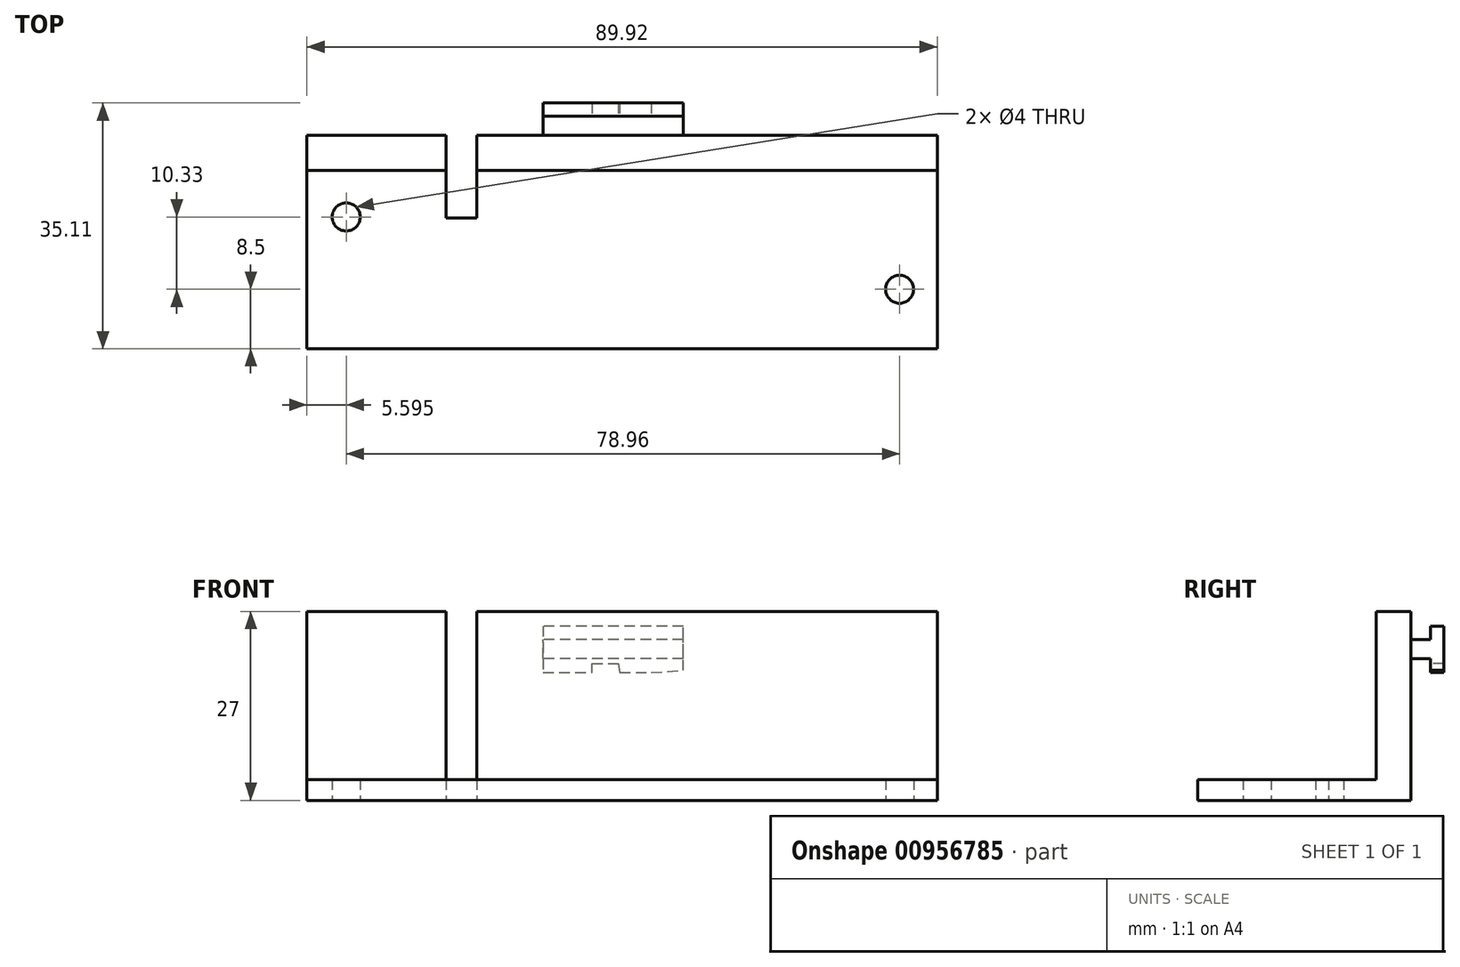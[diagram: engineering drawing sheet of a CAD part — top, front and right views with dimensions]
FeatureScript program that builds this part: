
annotation { "Feature Type Name" : "Feature", "Feature Type Description" : "" }
export const myFeature = defineFeature(function(context is Context, id is Id, definition is map)
    precondition{}
    {
        {
            var Q0;
            Q0=qCreatedBy(makeId("Top.planeOp"),FACE);
            var sketch = newSketch(context, id + "F0", { "sketchPlane" : qUnion([Q0])});
            skLineSegment(sketch, "E0.bottom", {"start": v(44.97, -13.73) * mm, "end": v(-44.97, -13.73) * mm});
            skLineSegment(sketch, "E0.top", {"start": v(44.97, 13.73) * mm, "end": v(-20.76, 13.73) * mm});
            skLineSegment(sketch, "E0.left", {"start": v(44.97, -13.73) * mm, "end": v(44.97, 13.73) * mm});
            skLineSegment(sketch, "E0.right", {"start": v(-44.97, -13.73) * mm, "end": v(-44.97, 13.73) * mm});
            skPoint(sketch, "E0.middle", {"position": v(0, 0) * mm});
            skLineSegment(sketch, "E1", {"start": v(-20.76, 13.73) * mm, "end": v(-20.76, 4.94) * mm});
            skLineSegment(sketch, "E2", {"start": v(-20.76, 4.94) * mm, "end": v(-25.1, 4.94) * mm});
            skLineSegment(sketch, "E3", {"start": v(-25.1, 4.94) * mm, "end": v(-25.1, 13.73) * mm});
            skLineSegment(sketch, "E4.trimOffspring", {"start": v(-25.1, 13.73) * mm, "end": v(-44.97, 13.73) * mm});
            skCircle(sketch, "E5", {"center": v(39.6, -5.23) * mm, "radius": 2 * mm});
            skCircle(sketch, "E6", {"center": v(-39.37, 5.1) * mm, "radius": 2 * mm});
            skSolve(sketch);
        }
        {
            var Q0;
            Q0=makeQuery(id+"F0.imprint","IMPRINT",FACE,{"disambiguationData":[TD([[makeQuery(id+"F0.imprint","IMPRINT",EDGE,{"derivedFrom":sQuery(id+"F0.wireOp",EDGE,"E0.bottom")}),-1.0]])]});
            extrude(context, id + "F1", {"entities" : qUnion([Q0]), "depth" : 3 * mm, "offsetDistance" : 25 * mm});
        }
        {
            var Q0;
            Q0=makeQuery(id+"F1.opExtrude","SWEPT_FACE",FACE,{"disambiguationData":[OSD([sQuery(id+"F0.wireOp",EDGE,"E4.trimOffspring")])]});
            var sketch = newSketch(context, id + "F2", { "sketchPlane" : qUnion([Q0])});
            skLineSegment(sketch, "E7.0", {"start": v(25.1, 0) * mm, "end": v(44.97, 0) * mm});
            skLineSegment(sketch, "E7.1", {"start": v(25.1, 3) * mm, "end": v(44.97, 3) * mm});
            skLineSegment(sketch, "E8", {"start": v(-8.73, 0) * mm, "end": v(-8.73, 3) * mm});
            skLineSegment(sketch, "E9", {"start": v(11.27, 0) * mm, "end": v(11.27, 3) * mm});
            skLineSegment(sketch, "E10.0", {"start": v(-44.97, 3) * mm, "end": v(-44.97, 0) * mm});
            skLineSegment(sketch, "E11.0", {"start": v(44.97, 3) * mm, "end": v(44.97, 0) * mm});
            skLineSegment(sketch, "E12.0", {"start": v(20.76, 0) * mm, "end": v(25.1, 0) * mm});
            skLineSegment(sketch, "E13.0", {"start": v(-44.97, 0) * mm, "end": v(20.76, 0) * mm});
            skLineSegment(sketch, "E14", {"start": v(44.97, 3) * mm, "end": v(44.97, 27) * mm});
            skLineSegment(sketch, "E15", {"start": v(44.97, 27) * mm, "end": v(-44.97, 27) * mm});
            skLineSegment(sketch, "E16", {"start": v(-44.97, 27) * mm, "end": v(-44.97, 3) * mm});
            skLineSegment(sketch, "E17.0", {"start": v(20.76, 3) * mm, "end": v(25.1, 3) * mm});
            skLineSegment(sketch, "E18.0", {"start": v(20.76, 3) * mm, "end": v(20.76, 0) * mm});
            skLineSegment(sketch, "E19", {"start": v(20.76, 3) * mm, "end": v(20.76, 27) * mm});
            skLineSegment(sketch, "E20", {"start": v(25.1, 3) * mm, "end": v(25.1, 27) * mm});
            skSolve(sketch);
        }
        {
            var Q0;
            {var subQ3=sQuery(id+"F2.wireOp",EDGE,"E10.0");Q0=makeQuery(id+"F2.imprint","IMPRINT",FACE,{"disambiguationData":[TD([[makeQuery(id+"F2.imprint","IMPRINT",EDGE,{"derivedFrom":subQ3}),1.0]])]});}
            var Q1;
            Q1=makeQuery(id+"F2.imprint","IMPRINT",FACE,{"disambiguationData":[TD([[makeQuery(id+"F2.imprint","IMPRINT",EDGE,{"derivedFrom":sQuery(id+"F2.wireOp",EDGE,"E7.1")}),1.0]])]});
            var Q2;
            Q2=makeQuery(id+"F2.imprint","IMPRINT",FACE,{"disambiguationData":[TD([[makeQuery(id+"F2.imprint","IMPRINT",EDGE,{"derivedFrom":sQuery(id+"F2.wireOp",EDGE,"E7.0")}),1.0]])]});
            extrude(context, id + "F3", {"entities" : qUnion([Q0, Q1, Q2]), "operationType" : NewBodyOperationType.ADD, "depth" : 3 * mm, "offsetDistance" : 25 * mm});
        }
        {
            var Q0;
            Q0=makeQuery(id+"F3.opExtrude","CAP_FACE",FACE,{"disambiguationData":[OSD([sQuery(id+"F0.wireOp",EDGE,"E3"),sQuery(id+"F0.wireOp",EDGE,"E4.trimOffspring"),sQuery(id+"F2.wireOp",EDGE,"E7.0"),sQuery(id+"F2.wireOp",EDGE,"E11.0"),sQuery(id+"F2.wireOp",EDGE,"E14"),sQuery(id+"F2.wireOp",EDGE,"E15"),sQuery(id+"F2.wireOp",EDGE,"E20")])],"isStart":false});
            var sketch = newSketch(context, id + "F4", { "sketchPlane" : qUnion([Q0])});
            skLineSegment(sketch, "E21.0", {"start": v(-8.73, 0) * mm, "end": v(-8.73, 3) * mm});
            skLineSegment(sketch, "E22.0", {"start": v(11.27, 0) * mm, "end": v(11.27, 3) * mm});
            skLineSegment(sketch, "E23", {"start": v(-8.73, 3) * mm, "end": v(-8.73, 27) * mm});
            skLineSegment(sketch, "E24", {"start": v(11.27, 3) * mm, "end": v(11.27, 27) * mm});
            skLineSegment(sketch, "E25", {"start": v(11.27, 27) * mm, "end": v(-8.73, 27) * mm});
            skLineSegment(sketch, "E26", {"start": v(-8.73, 23) * mm, "end": v(11.27, 23) * mm});
            skLineSegment(sketch, "E27", {"start": v(-8.73, 20.25) * mm, "end": v(11.27, 20.25) * mm});
            skSolve(sketch);
        }
        {
            var Q0;
            {var subQ0=sQuery(id+"F4.wireOp",EDGE,"E26");Q0=makeQuery(id+"F4.imprint","IMPRINT",FACE,{"disambiguationData":[TD([[makeQuery(id+"F4.imprint","IMPRINT",EDGE,{"derivedFrom":subQ0}),-1.0]])]});}
            extrude(context, id + "F5", {"entities" : qUnion([Q0]), "operationType" : NewBodyOperationType.ADD, "depth" : 2.75 * mm, "offsetDistance" : 25 * mm});
        }
        {
            var Q0;
            Q0=makeQuery(id+"F5.opExtrude","CAP_FACE",FACE,{"disambiguationData":[OSD([sQuery(id+"F4.wireOp",EDGE,"E23"),sQuery(id+"F4.wireOp",EDGE,"E24"),sQuery(id+"F4.wireOp",EDGE,"E26"),sQuery(id+"F4.wireOp",EDGE,"E27")])],"isStart":false});
            var sketch = newSketch(context, id + "F6", { "sketchPlane" : qUnion([Q0])});
            skLineSegment(sketch, "E28.0", {"start": v(-8.73, 20.25) * mm, "end": v(-8.73, 23) * mm});
            skLineSegment(sketch, "E29.0", {"start": v(11.27, 20.25) * mm, "end": v(11.27, 23) * mm});
            skLineSegment(sketch, "E30", {"start": v(11.27, 20.25) * mm, "end": v(11.27, 18.27) * mm});
            skLineSegment(sketch, "E31", {"start": v(11.27, 18.27) * mm, "end": v(-4.16, 18.27) * mm});
            skLineSegment(sketch, "E32", {"start": v(-8.73, 18.57) * mm, "end": v(-8.73, 20.25) * mm});
            skLineSegment(sketch, "E33", {"start": v(-8.73, 23) * mm, "end": v(-8.73, 24.9) * mm});
            skLineSegment(sketch, "E34", {"start": v(-8.73, 24.9) * mm, "end": v(11.27, 24.9) * mm});
            skLineSegment(sketch, "E35", {"start": v(11.27, 24.9) * mm, "end": v(11.27, 21.62) * mm});
            skLineSegment(sketch, "E36", {"start": v(4.27, 18.27) * mm, "end": v(4.27, 19.52) * mm});
            skLineSegment(sketch, "E37", {"start": v(4.27, 19.52) * mm, "end": v(0.52, 19.52) * mm});
            skLineSegment(sketch, "E38", {"start": v(0.52, 19.52) * mm, "end": v(0.32, 18.27) * mm});
            skLineSegment(sketch, "E39", {"start": v(-4.16, 18.27) * mm, "end": v(-8.73, 18.57) * mm});
            skPoint(sketch, "E40.orphan", {"position": v(-8.73, 18.27) * mm});
            skSolve(sketch);
        }
        {
            var Q0;
            {var subQ3=sQuery(id+"F6.wireOp",EDGE,"E30");Q0=makeQuery(id+"F6.imprint","IMPRINT",FACE,{"disambiguationData":[TD([[makeQuery(id+"F6.imprint","IMPRINT",EDGE,{"derivedFrom":subQ3}),-1.0]])]});}
            var Q1;
            Q1=makeQuery(id+"F6.imprint","IMPRINT",FACE,{"disambiguationData":[TD([[makeQuery(id+"F6.imprint","IMPRINT",EDGE,{"derivedFrom":sQuery(id+"F6.wireOp",EDGE,"E28.0")}),-1.0]])]});
            var Q2;
            Q2=makeQuery(id+"F6.imprint","IMPRINT",FACE,{"disambiguationData":[TD([[makeQuery(id+"F6.imprint","IMPRINT",EDGE,{"derivedFrom":sQuery(id+"F6.wireOp",EDGE,"E33")}),-1.0]])]});
            extrude(context, id + "F7", {"entities" : qUnion([Q0, Q1, Q2]), "operationType" : NewBodyOperationType.ADD, "depth" : 1.9 * mm, "offsetDistance" : 25 * mm});
        }
        {
            var Q0;
            Q0=makeQuery(id+"F2.imprint","IMPRINT",FACE,{"disambiguationData":[TD([[makeQuery(id+"F2.imprint","IMPRINT",EDGE,{"derivedFrom":sQuery(id+"F2.wireOp",EDGE,"E7.1")}),1.0]])]});
            var Q1;
            {var subQ3=sQuery(id+"F2.wireOp",EDGE,"E10.0");Q1=makeQuery(id+"F2.imprint","IMPRINT",FACE,{"disambiguationData":[TD([[makeQuery(id+"F2.imprint","IMPRINT",EDGE,{"derivedFrom":subQ3}),1.0]])]});}
            extrude(context, id + "F8", {"entities" : qUnion([Q0, Q1]), "operationType" : NewBodyOperationType.ADD, "oppositeDirection" : true, "depth" : 2 * mm, "offsetDistance" : 25 * mm});
        }
    });
